# Revit family: FONESTAR_Altavoz_Techo
name_source: partatom
category: Communication Devices
units: mm (PartAtom-declared; Revit-internal decimal feet)

## family parameters
Cut with Voids When Loaded = No
Host = Face
Maintain Annotation Orientation = No
Part Type = Normal
Room Calculation Point = No
Round Connector Dimension = Use Diameter
Shared = No

## types (6) — shared parameters
Default Elevation = 1000 mm
Manufacturer = FONESTAR
Modified by = XPV
Protección IP = -
Reviewed by = TAG
Sujección.Diámetro = 20 mm  [stored 0.0656168 ft]
URL = https://fonestar.com
URL.Product = https://fonestar.com
Version = R0

## per-type parameters (varying)
- GAT-252: Altura=76 mm  [stored 0.249344 ft]; Cuerpo=Yes; Cuerpo.Altura.Inferior=11 mm; Cuerpo.Altura.Medio=46 mm  [stored 0.150919 ft]; Cuerpo.Altura.Superior=19 mm  [stored 0.062336 ft]; Cuerpo.Dimensión=69 mm  [stored 0.226378 ft]; Cuerpo.Diámetro.Inferior=87 mm  [stored 0.285433 ft]; Cuerpo.Diámetro.Superior=65 mm; Cuerpo.M01=No; Cuerpo.M02=No; Cuerpo.Material=Plástico ABS - Blanco RAL(9003); Description=Altavoz de techo con transformador de línea 100 V. Tamaño foco halógeno. Sistema de instalación rápida.; Diámetro=104 mm; Diámetro.Orificio=92 mm  [stored 0.301837 ft]; Embellecedor.Diámetro.Interior=102 mm; Embellecedor.Espesor=2 mm  [stored 0.00656168 ft]; Embellecedor.Material=Plástico ABS - Blanco RAL(9003); Material.Iman=Aluminio_Rejilla - Blanco RAL(9003); Peso=0,42 Kg; Potencia.Acústica=6 W RMS; Rejilla.Curva.Espesor=2 mm  [stored 0.00656168 ft]; Rejilla.Espesor=2 mm  [stored 0.00656168 ft]; Rejilla.Material=Aluminio_Rejilla - Blanco RAL(9003); Respuesta Acústica=120-12.000 Hz; Sujección.Dimensión=52 mm
- GAT-4509: Altura=80 mm  [stored 0.262467 ft]; Cuerpo=No; Cuerpo.Altura.Inferior=12 mm  [stored 0.0393701 ft]; Cuerpo.Altura.Medio=48 mm  [stored 0.15748 ft]; Cuerpo.Altura.Superior=20 mm  [stored 0.0656168 ft]; Cuerpo.Dimensión=87 mm  [stored 0.285433 ft]; Cuerpo.Diámetro.Inferior=165 mm  [stored 0.541339 ft]; Cuerpo.Diámetro.Superior=124 mm; Cuerpo.M01=Yes; Cuerpo.M02=No; Cuerpo.Material=Plástico ABS - Blanco RAL(9010); Description=Altavoz de techo con transformador de línea 100 V. Rejilla redonda de bajo perfil sin marco. Altura de rejilla 6 mm. Marco de 1 mm de ancho.; Diámetro=191 mm; Diámetro.Orificio=170 mm  [stored 0.557743 ft]; Embellecedor.Diámetro.Interior=189 mm; Embellecedor.Espesor=6 mm  [stored 0.019685 ft]; Embellecedor.Material=Plástico ABS - Blanco RAL(9010); Material.Iman=Aluminio; Peso=1 Kg; Potencia.Acústica=10 W RMS; Rejilla.Curva.Espesor=6 mm  [stored 0.019685 ft]; Rejilla.Espesor=6 mm  [stored 0.019685 ft]; Rejilla.Material=Aluminio_Rejilla - Blanco RAL(9010); Respuesta Acústica=90-20.000 Hz; Sujección.Dimensión=96 mm  [stored 0.314961 ft]
- GAT-4507: Altura=70 mm  [stored 0.229659 ft]; Cuerpo=No; Cuerpo.Altura.Inferior=11 mm; Cuerpo.Altura.Medio=42 mm  [stored 0.137795 ft]; Cuerpo.Altura.Superior=18 mm; Cuerpo.Dimensión=87 mm  [stored 0.285433 ft]; Cuerpo.Diámetro.Inferior=165 mm  [stored 0.541339 ft]; Cuerpo.Diámetro.Superior=124 mm; Cuerpo.M01=Yes; Cuerpo.M02=No; Cuerpo.Material=Plástico ABS - Blanco RAL(9010); Description=Altavoz de techo con transformador de línea 100 V. Rejilla redonda de bajo perfil sin marco. Altura de rejilla 6 mm. Marco de 1 mm de ancho.; Diámetro=192 mm; Diámetro.Orificio=170 mm  [stored 0.557743 ft]; Embellecedor.Diámetro.Interior=190 mm; Embellecedor.Espesor=6 mm  [stored 0.019685 ft]; Embellecedor.Material=Plástico ABS - Blanco RAL(9010); Material.Iman=Aluminio; Peso=0,6 Kg; Potencia.Acústica=7 W RMS; Rejilla.Curva.Espesor=6 mm  [stored 0.019685 ft]; Rejilla.Espesor=6 mm  [stored 0.019685 ft]; Rejilla.Material=Aluminio_Rejilla - Blanco RAL(9010); Respuesta Acústica=110-15.000 Hz; Sujección.Dimensión=96 mm  [stored 0.314961 ft]
- GAT-4510: Altura=94 mm  [stored 0.308399 ft]; Cuerpo=No; Cuerpo.Altura.Inferior=14 mm  [stored 0.0459318 ft]; Cuerpo.Altura.Medio=56 mm; Cuerpo.Altura.Superior=24 mm; Cuerpo.Dimensión=87 mm  [stored 0.285433 ft]; Cuerpo.Diámetro.Inferior=182 mm; Cuerpo.Diámetro.Superior=137 mm; Cuerpo.M01=No; Cuerpo.M02=Yes; Cuerpo.Material=Auxiliar - Negro; Description=Altavoz de techo con transformador de línea 100 V. Rejilla redonda de bajo perfil sin marco. Altura de rejilla 5 mm. Marco de 1 mm de ancho.; Diámetro=217 mm; Diámetro.Orificio=187 mm; Embellecedor.Diámetro.Interior=215 mm; Embellecedor.Espesor=5 mm  [stored 0.0164042 ft]; Embellecedor.Material=Plástico ABS - Blanco RAL(9010); Material.Iman=Aluminio; Peso=1,4 Kg; Potencia.Acústica=10 W RMS; Rejilla.Curva.Espesor=5 mm  [stored 0.0164042 ft]; Rejilla.Espesor=5 mm  [stored 0.0164042 ft]; Rejilla.Material=Aluminio_Rejilla - Blanco RAL(9010); Respuesta Acústica=55-20.000 Hz; Sujección.Dimensión=109 mm
- GAT-4620: Altura=87 mm  [stored 0.285433 ft]; Cuerpo=No; Cuerpo.Altura.Inferior=13 mm; Cuerpo.Altura.Medio=52 mm; Cuerpo.Altura.Superior=22 mm; Cuerpo.Dimensión=87 mm  [stored 0.285433 ft]; Cuerpo.Diámetro.Inferior=209 mm; Cuerpo.Diámetro.Superior=157 mm; Cuerpo.M01=No; Cuerpo.M02=Yes; Cuerpo.Material=Auxiliar - Negro; Description=Altavoz de techo con transformador de línea 100 V. Rejilla redonda de bajo perfil sin marco. Altura de rejilla 5 mm. Marco de 1 mm de ancho.; Diámetro=246 mm; Diámetro.Orificio=214 mm; Embellecedor.Diámetro.Interior=244 mm; Embellecedor.Espesor=5 mm  [stored 0.0164042 ft]; Embellecedor.Material=Plástico ABS - Blanco RAL(9010); Material.Iman=Aluminio; Peso=1,6 Kg; Potencia.Acústica=20 W RMS; Rejilla.Curva.Espesor=5 mm  [stored 0.0164042 ft]; Rejilla.Espesor=5 mm  [stored 0.0164042 ft]; Rejilla.Material=Aluminio_Rejilla - Blanco RAL(9010); Respuesta Acústica=45-20.000 Hz; Sujección.Dimensión=123 mm  [stored 0.403543 ft]
- GAT-4860SW: Altura=110 mm  [stored 0.360892 ft]; Cuerpo=No; Cuerpo.Altura.Inferior=17 mm; Cuerpo.Altura.Medio=66 mm  [stored 0.216535 ft]; Cuerpo.Altura.Superior=28 mm; Cuerpo.Dimensión=87 mm  [stored 0.285433 ft]; Cuerpo.Diámetro.Inferior=237 mm; Cuerpo.Diámetro.Superior=178 mm; Cuerpo.M01=No; Cuerpo.M02=Yes; Cuerpo.Material=Auxiliar - Negro; Description=Altavoz de techo subwoofer con transformador de línea 100 V y rejilla sin marco de bajo perfil.
Refuerzo de graves en instalaciones de línea 100 V.; Diámetro=282 mm; Diámetro.Orificio=242 mm; Embellecedor.Diámetro.Interior=280 mm; Embellecedor.Espesor=5 mm  [stored 0.0164042 ft]; Embellecedor.Material=Plástico ABS - Blanco RAL(9003); Material.Iman=Aluminio; Peso=2,7 Kg; Potencia.Acústica=60 W RMS; Rejilla.Curva.Espesor=5 mm  [stored 0.0164042 ft]; Rejilla.Espesor=5 mm  [stored 0.0164042 ft]; Rejilla.Material=Aluminio_Rejilla - Blanco RAL(9003); Respuesta Acústica=55-20.000 Hz; Sujección.Dimensión=141 mm

note: column(s) folded — value = type name in every type: Model

note: [stored X ft] marks values corroborated as IEEE doubles in the binary element streams (Revit-internal decimal feet)
